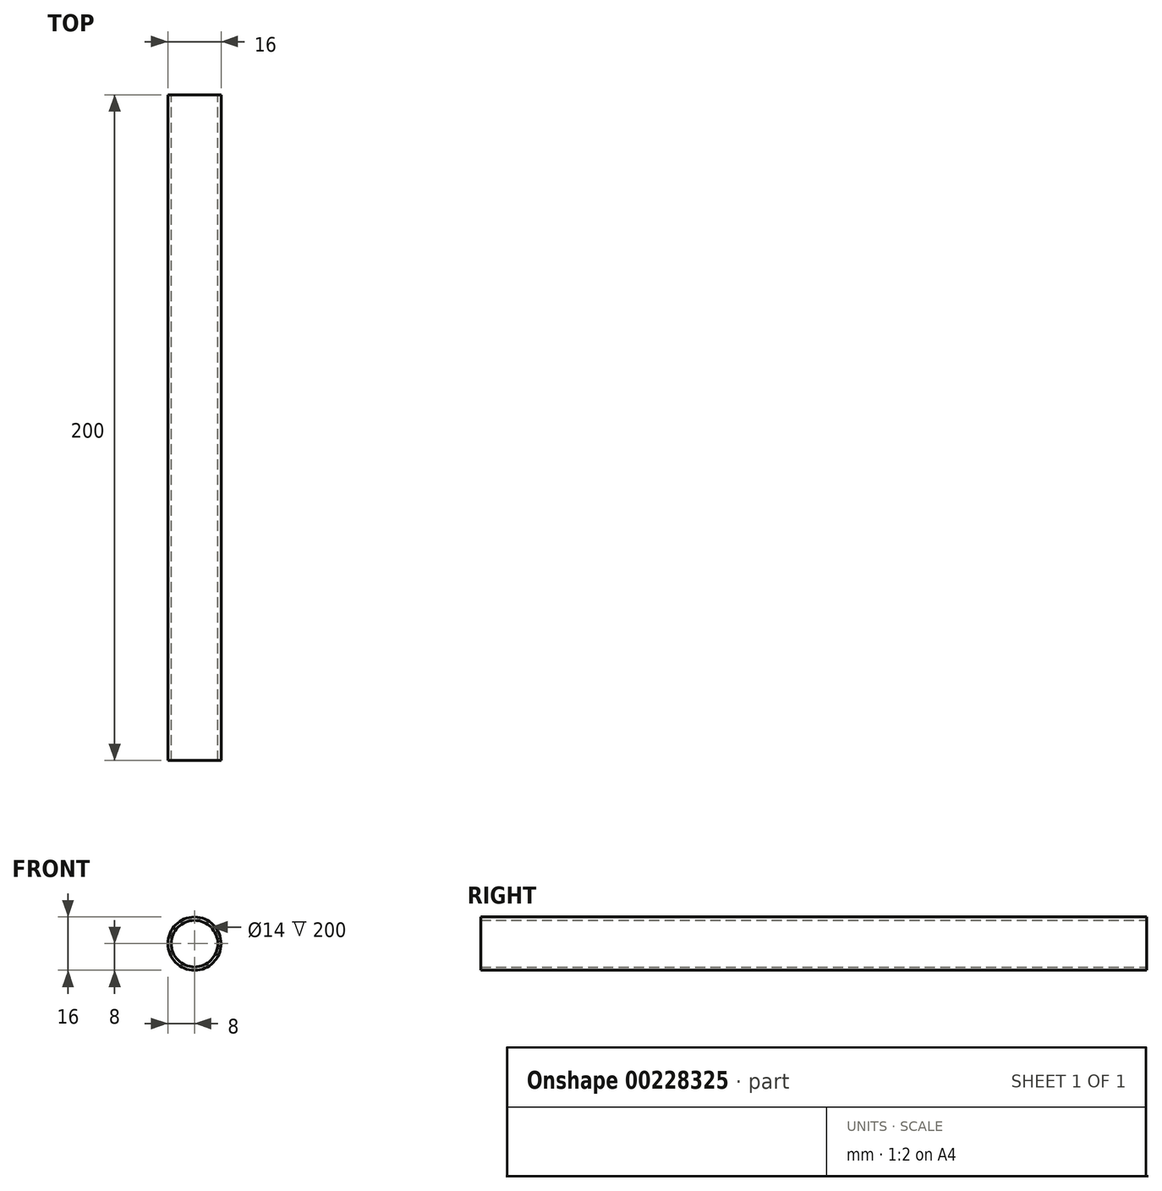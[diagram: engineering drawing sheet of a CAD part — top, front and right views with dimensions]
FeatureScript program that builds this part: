
annotation { "Feature Type Name" : "Feature", "Feature Type Description" : "" }
export const myFeature = defineFeature(function(context is Context, id is Id, definition is map)
    precondition{}
    {
        {
            var Q0;
            Q0=qCreatedBy(makeId("Front.planeOp"),FACE);
            var sketch = newSketch(context, id + "F0", { "sketchPlane" : qUnion([Q0])});
            skCircle(sketch, "E0", {"center": v(0, 0) * mm, "radius": 8 * mm});
            skCircle(sketch, "E1", {"center": v(0, 0) * mm, "radius": 7 * mm});
            skSolve(sketch);
        }
        {
            var Q0;
            Q0=makeQuery(id+"F0.imprint","IMPRINT",FACE,{"disambiguationData":[TD([[makeQuery(id+"F0.imprint","IMPRINT",EDGE,{"derivedFrom":sQuery(id+"F0.wireOp",EDGE,"E0")}),1.0]])]});
            extrude(context, id + "F1", {"entities" : qUnion([Q0]), "depth" : 200 * mm});
        }
    });
